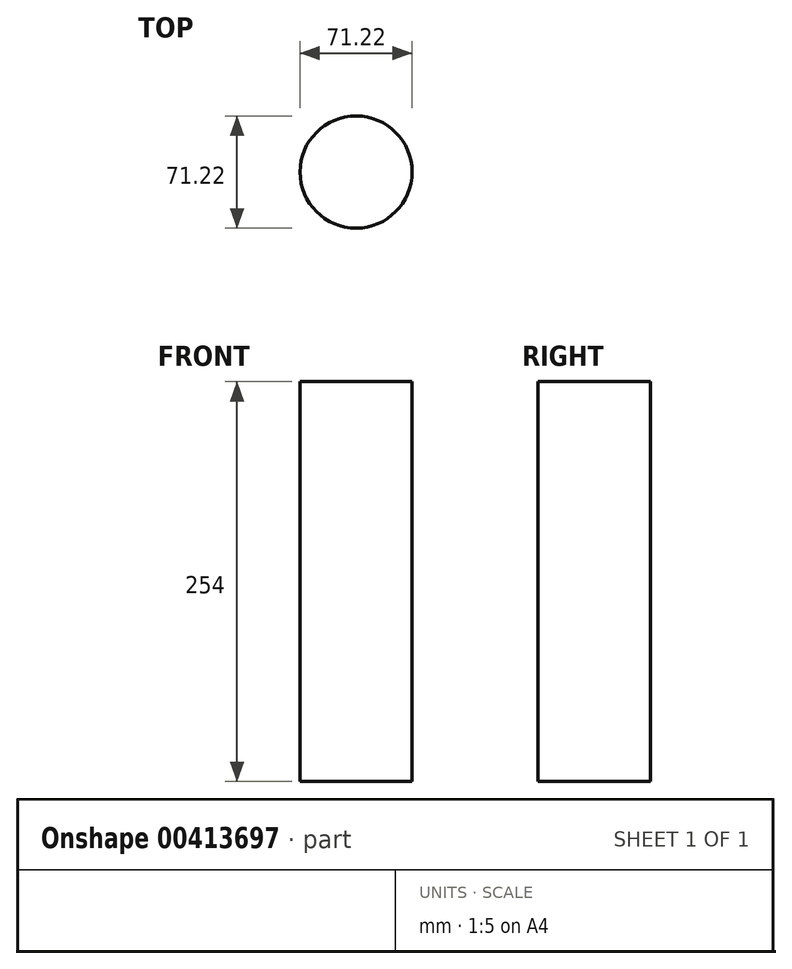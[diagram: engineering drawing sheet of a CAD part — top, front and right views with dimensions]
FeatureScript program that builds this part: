
annotation { "Feature Type Name" : "Feature", "Feature Type Description" : "" }
export const myFeature = defineFeature(function(context is Context, id is Id, definition is map)
    precondition{}
    {
        {
            var Q0;
            Q0=qCreatedBy(makeId("Top.planeOp"),FACE);
            var sketch = newSketch(context, id + "F0", { "sketchPlane" : qUnion([Q0])});
            skCircle(sketch, "E0", {"center": v(0, 0) * mm, "radius": 35.6 * mm});
            skSolve(sketch);
        }
        {
            var Q0;
            Q0=makeQuery(id+"F0.imprint","IMPRINT",FACE,{"disambiguationData":[TD([[makeQuery(id+"F0.imprint","IMPRINT",EDGE,{"derivedFrom":sQuery(id+"F0.wireOp",EDGE,"E0")}),1.0]])]});
            var Q1;
            Q1=sQuery(id+"F0.wireOp",EDGE,"E0");
            extrude(context, id + "F1", {"entities" : qUnion([Q0]), "surfaceEntities" : qUnion([Q1]), "depth" : 254 * mm});
        }
    });
